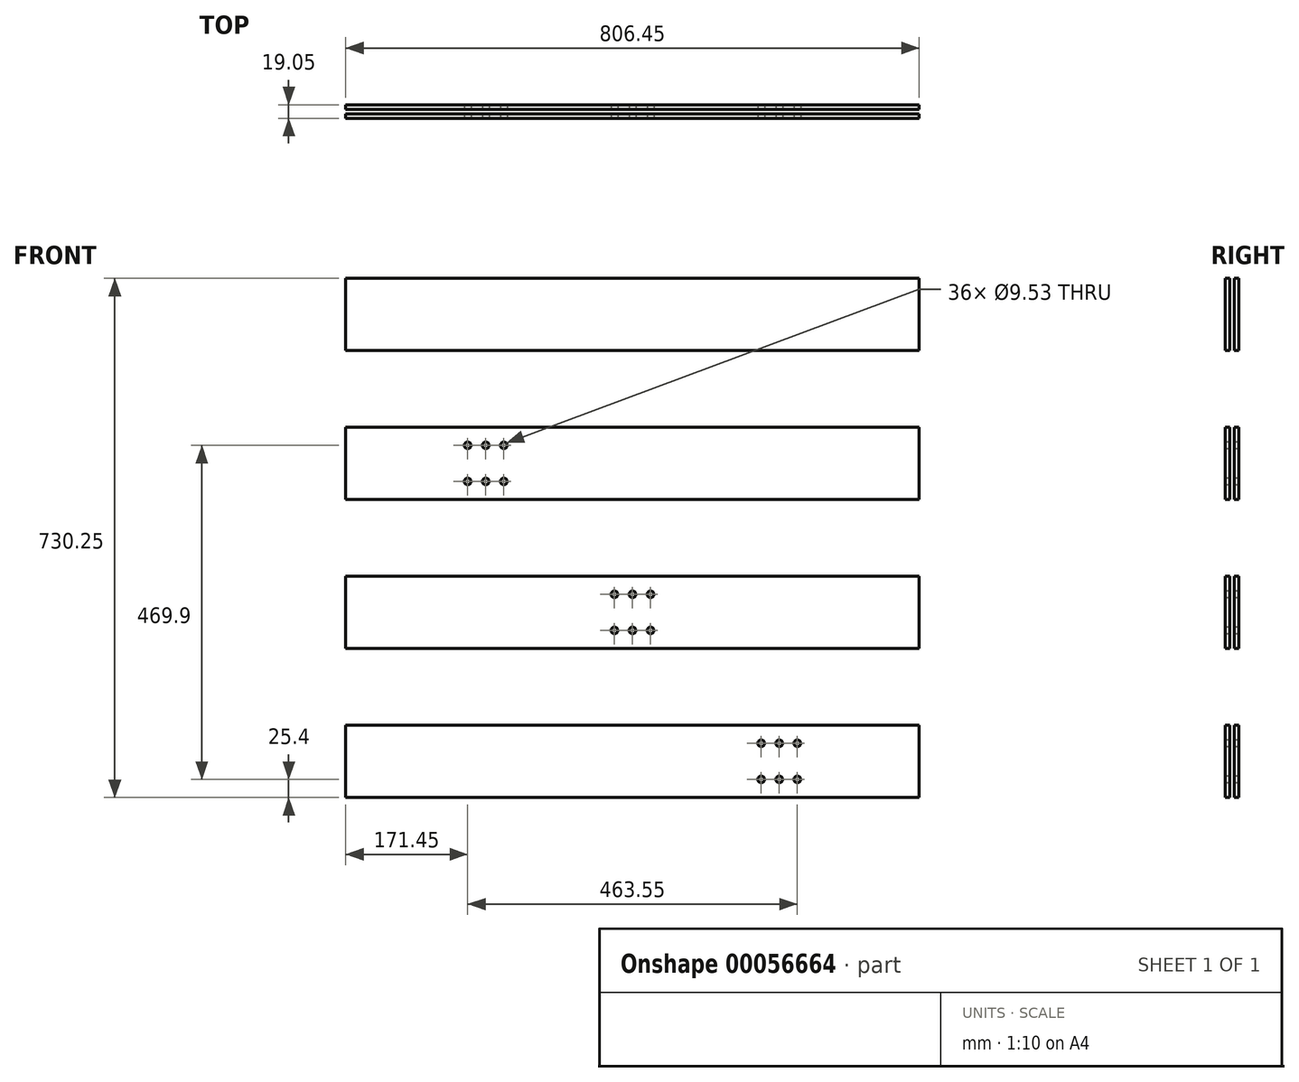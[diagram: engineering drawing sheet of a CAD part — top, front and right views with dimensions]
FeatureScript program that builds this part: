
annotation { "Feature Type Name" : "Feature", "Feature Type Description" : "" }
export const myFeature = defineFeature(function(context is Context, id is Id, definition is map)
    precondition{}
    {
        {
            var Q0;
            Q0=qCreatedBy(makeId("Right.planeOp"),FACE);
            cPlane(context, id + "F0", {"entities" : qUnion([Q0]), "cplaneType" : CPlaneType.OFFSET, "offset" : 76.2 * mm, "width" : 152.4 * mm, "height" : 152.4 * mm});
        }
        {
            var Q0;
            Q0=qCreatedBy(id+"F0.planeOp",FACE);
            var sketch = newSketch(context, id + "F1", { "sketchPlane" : qUnion([Q0])});
            skLineSegment(sketch, "E0.bottom", {"start": v(635, 1346.2) * mm, "end": v(641.35, 1346.2) * mm});
            skLineSegment(sketch, "E0.top", {"start": v(635, 1244.6) * mm, "end": v(641.35, 1244.6) * mm});
            skLineSegment(sketch, "E0.left", {"start": v(635, 1346.2) * mm, "end": v(635, 1244.6) * mm});
            skLineSegment(sketch, "E0.right", {"start": v(641.35, 1346.2) * mm, "end": v(641.35, 1244.6) * mm});
            skLineSegment(sketch, "E1.bottom", {"start": v(635, 1136.65) * mm, "end": v(641.35, 1136.65) * mm});
            skLineSegment(sketch, "E1.top", {"start": v(635, 1035.05) * mm, "end": v(641.35, 1035.05) * mm});
            skLineSegment(sketch, "E1.left", {"start": v(635, 1136.65) * mm, "end": v(635, 1035.05) * mm});
            skLineSegment(sketch, "E1.right", {"start": v(641.35, 1136.65) * mm, "end": v(641.35, 1035.05) * mm});
            skLineSegment(sketch, "E2.bottom", {"start": v(635, 927.1) * mm, "end": v(641.35, 927.1) * mm});
            skLineSegment(sketch, "E2.top", {"start": v(635, 825.5) * mm, "end": v(641.35, 825.5) * mm});
            skLineSegment(sketch, "E2.left", {"start": v(635, 927.1) * mm, "end": v(635, 825.5) * mm});
            skLineSegment(sketch, "E2.right", {"start": v(641.35, 927.1) * mm, "end": v(641.35, 825.5) * mm});
            skLineSegment(sketch, "E3.bottom", {"start": v(635, 717.55) * mm, "end": v(641.35, 717.55) * mm});
            skLineSegment(sketch, "E3.top", {"start": v(635, 615.95) * mm, "end": v(641.35, 615.95) * mm});
            skLineSegment(sketch, "E3.left", {"start": v(635, 717.55) * mm, "end": v(635, 615.95) * mm});
            skLineSegment(sketch, "E3.right", {"start": v(641.35, 717.55) * mm, "end": v(641.35, 615.95) * mm});
            skLineSegment(sketch, "E4.1.0.0", {"start": v(654.05, 927.1) * mm, "end": v(654.05, 825.5) * mm});
            skLineSegment(sketch, "E4.1.0.1", {"start": v(647.7, 927.1) * mm, "end": v(647.7, 825.5) * mm});
            skLineSegment(sketch, "E4.1.0.2", {"start": v(654.05, 1136.65) * mm, "end": v(654.05, 1035.05) * mm});
            skLineSegment(sketch, "E4.1.0.3", {"start": v(647.7, 1136.65) * mm, "end": v(647.7, 1035.05) * mm});
            skLineSegment(sketch, "E4.1.0.4", {"start": v(654.05, 1346.2) * mm, "end": v(654.05, 1244.6) * mm});
            skLineSegment(sketch, "E4.1.0.5", {"start": v(647.7, 1346.2) * mm, "end": v(647.7, 1244.6) * mm});
            skLineSegment(sketch, "E4.1.0.6", {"start": v(654.05, 717.55) * mm, "end": v(654.05, 615.95) * mm});
            skLineSegment(sketch, "E4.1.0.7", {"start": v(647.7, 717.55) * mm, "end": v(647.7, 615.95) * mm});
            skLineSegment(sketch, "E4.1.0.8", {"start": v(647.7, 717.55) * mm, "end": v(654.05, 717.55) * mm});
            skLineSegment(sketch, "E4.1.0.9", {"start": v(647.7, 825.5) * mm, "end": v(654.05, 825.5) * mm});
            skLineSegment(sketch, "E4.1.0.10", {"start": v(647.7, 927.1) * mm, "end": v(654.05, 927.1) * mm});
            skLineSegment(sketch, "E4.1.0.11", {"start": v(647.7, 1136.65) * mm, "end": v(654.05, 1136.65) * mm});
            skLineSegment(sketch, "E4.1.0.12", {"start": v(647.7, 1244.6) * mm, "end": v(654.05, 1244.6) * mm});
            skLineSegment(sketch, "E4.1.0.13", {"start": v(647.7, 1346.2) * mm, "end": v(654.05, 1346.2) * mm});
            skLineSegment(sketch, "E4.1.0.14", {"start": v(647.7, 615.95) * mm, "end": v(654.05, 615.95) * mm});
            skLineSegment(sketch, "E4.1.0.15", {"start": v(647.7, 1035.05) * mm, "end": v(654.05, 1035.05) * mm});
            skLineSegment(sketch, "E4.direction1", {"start": v(641.35, 825.5) * mm, "end": v(654.05, 825.5) * mm, "construction": true});
            skSolve(sketch);
        }
        {
            var Q0;
            Q0 = qSketchRegion(id + "F1", true);
            extrude(context, id + "F2", {"entities" : qUnion([Q0]), "depth" : 806.45 * mm});
        }
        {
            var Q0;
            Q0=makeQuery(id+"F2.opExtrude","SWEPT_FACE",FACE,{"disambiguationData":[OSD([sQuery(id+"F1.wireOp",EDGE,"E0.left")])]});
            var sketch = newSketch(context, id + "F3", { "sketchPlane" : qUnion([Q0])});
            skCircle(sketch, "E5", {"center": v(660.4, 692.15) * mm, "radius": 4.76 * mm});
            skCircle(sketch, "E6.0.1.0", {"center": v(660.4, 641.35) * mm, "radius": 4.76 * mm});
            skCircle(sketch, "E6.1.0.0", {"center": v(685.8, 692.15) * mm, "radius": 4.76 * mm});
            skCircle(sketch, "E6.1.1.0", {"center": v(685.8, 641.35) * mm, "radius": 4.76 * mm});
            skCircle(sketch, "E6.2.0.0", {"center": v(711.2, 692.15) * mm, "radius": 4.76 * mm});
            skCircle(sketch, "E6.2.1.0", {"center": v(711.2, 641.35) * mm, "radius": 4.76 * mm});
            skLineSegment(sketch, "E6.direction1", {"start": v(660.4, 692.15) * mm, "end": v(685.8, 692.15) * mm, "construction": true});
            skLineSegment(sketch, "E6.direction2", {"start": v(660.4, 692.15) * mm, "end": v(660.4, 641.35) * mm, "construction": true});
            skCircle(sketch, "E7", {"center": v(454.03, 901.7) * mm, "radius": 4.76 * mm});
            skCircle(sketch, "E8.0.1.0", {"center": v(454.03, 850.9) * mm, "radius": 4.76 * mm});
            skCircle(sketch, "E8.1.0.0", {"center": v(479.43, 901.7) * mm, "radius": 4.76 * mm});
            skCircle(sketch, "E8.1.1.0", {"center": v(479.43, 850.9) * mm, "radius": 4.76 * mm});
            skCircle(sketch, "E8.2.0.0", {"center": v(504.83, 901.7) * mm, "radius": 4.76 * mm});
            skCircle(sketch, "E8.2.1.0", {"center": v(504.83, 850.9) * mm, "radius": 4.76 * mm});
            skLineSegment(sketch, "E8.direction1", {"start": v(454.03, 901.7) * mm, "end": v(479.43, 901.7) * mm, "construction": true});
            skLineSegment(sketch, "E8.direction2", {"start": v(454.03, 901.7) * mm, "end": v(454.03, 850.9) * mm, "construction": true});
            skCircle(sketch, "E9", {"center": v(247.65, 1111.25) * mm, "radius": 4.76 * mm});
            skCircle(sketch, "E10.0.1.0", {"center": v(247.65, 1060.45) * mm, "radius": 4.76 * mm});
            skCircle(sketch, "E10.1.0.0", {"center": v(273.05, 1111.25) * mm, "radius": 4.76 * mm});
            skCircle(sketch, "E10.1.1.0", {"center": v(273.05, 1060.45) * mm, "radius": 4.76 * mm});
            skCircle(sketch, "E10.2.0.0", {"center": v(298.45, 1111.25) * mm, "radius": 4.76 * mm});
            skCircle(sketch, "E10.2.1.0", {"center": v(298.45, 1060.45) * mm, "radius": 4.76 * mm});
            skLineSegment(sketch, "E10.direction1", {"start": v(247.65, 1111.25) * mm, "end": v(273.05, 1111.25) * mm, "construction": true});
            skLineSegment(sketch, "E10.direction2", {"start": v(247.65, 1111.25) * mm, "end": v(247.65, 1060.45) * mm, "construction": true});
            skSolve(sketch);
        }
        {
            var Q0;
            Q0 = qSketchRegion(id + "F3", true);
            extrude(context, id + "F4", {"entities" : qUnion([Q0]), "operationType" : NewBodyOperationType.REMOVE, "endBound" : BoundingType.THROUGH_ALL, "oppositeDirection" : true, "depth" : 25.4 * mm});
        }
    });
